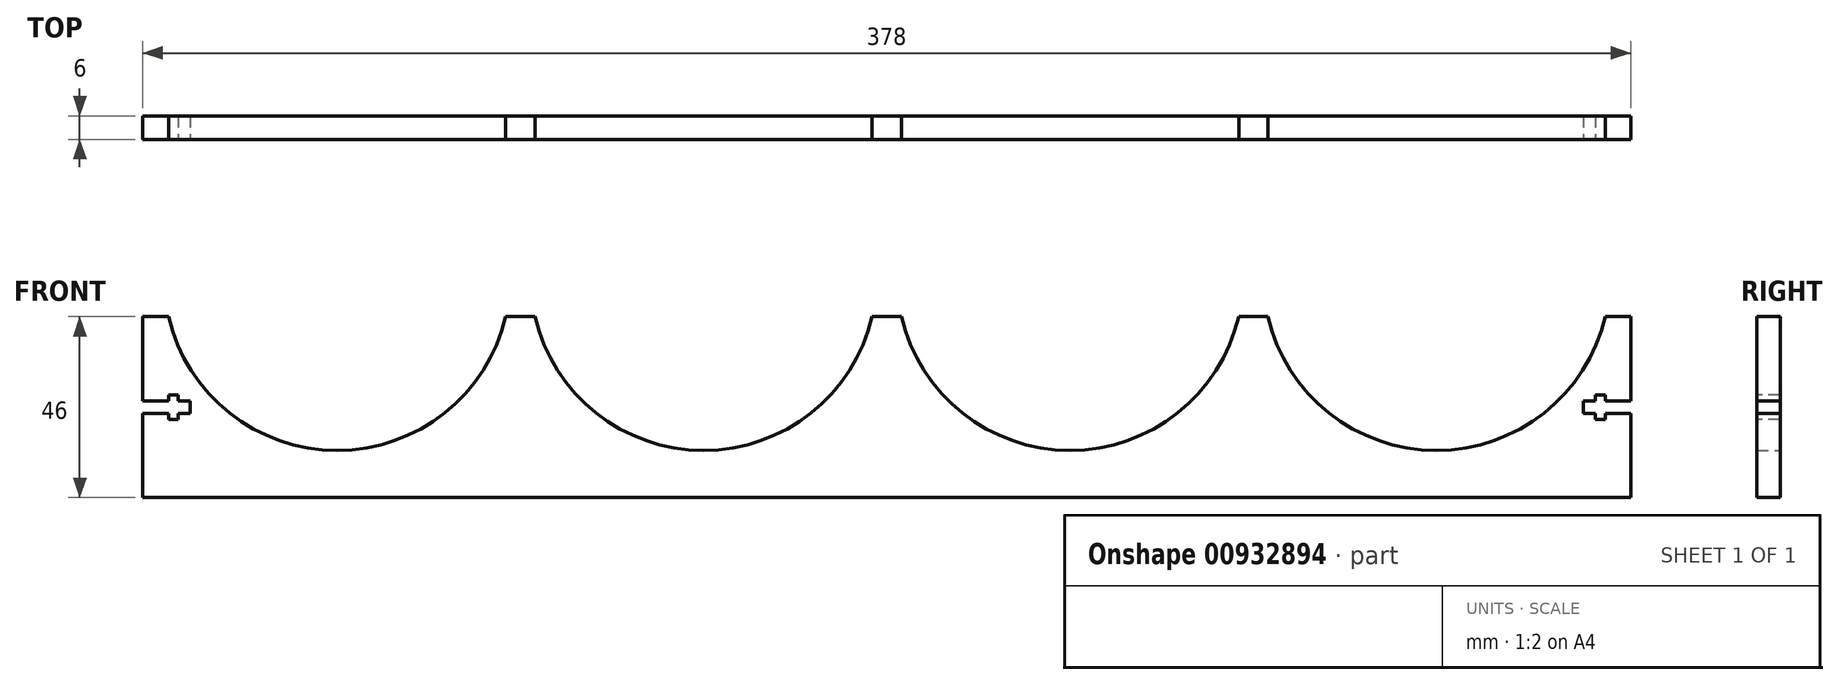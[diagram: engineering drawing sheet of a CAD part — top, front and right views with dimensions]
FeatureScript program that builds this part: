
annotation { "Feature Type Name" : "Feature", "Feature Type Description" : "" }
export const myFeature = defineFeature(function(context is Context, id is Id, definition is map)
    precondition{}
    {
        {
            var Q0;
            Q0=qCreatedBy(makeId("Front.planeOp"),FACE);
            var sketch = newSketch(context, id + "F0", { "sketchPlane" : qUnion([Q0])});
            skLineSegment(sketch, "E0.bottom", {"start": v(-189, 23) * mm, "end": v(-182.5, 23) * mm});
            skLineSegment(sketch, "E0.top", {"start": v(-189, -23) * mm, "end": v(189, -23) * mm});
            skLineSegment(sketch, "E0.left", {"start": v(-189, 23) * mm, "end": v(-189, -23) * mm});
            skLineSegment(sketch, "E0.right", {"start": v(189, 23) * mm, "end": v(189, -23) * mm});
            skLineSegment(sketch, "E1", {"start": v(0, 23) * mm, "end": v(0, 0) * mm, "construction": true});
            skLineSegment(sketch, "E2", {"start": v(0, 0) * mm, "end": v(-189, 0) * mm, "construction": true});
            skArc(sketch, "E3", {"start": v(-182.5, 23) * mm, "mid": v(-139.65, -11) * mm, "end": v(-96.8, 23) * mm});
            skArc(sketch, "E4", {"start": v(-89.4, 23) * mm, "mid": v(-46.55, -11) * mm, "end": v(-3.7, 23) * mm});
            skArc(sketch, "E5.MirrorCS", {"start": v(89.4, 23) * mm, "mid": v(46.55, -11) * mm, "end": v(3.7, 23) * mm});
            skArc(sketch, "E6.MirrorCS", {"start": v(182.5, 23) * mm, "mid": v(139.65, -11) * mm, "end": v(96.8, 23) * mm});
            skLineSegment(sketch, "E7.trimOffspring", {"start": v(-96.8, 23) * mm, "end": v(-89.4, 23) * mm});
            skLineSegment(sketch, "E8.trimOffspring", {"start": v(-3.7, 23) * mm, "end": v(3.7, 23) * mm});
            skLineSegment(sketch, "E9.trimOffspring", {"start": v(89.4, 23) * mm, "end": v(96.8, 23) * mm});
            skLineSegment(sketch, "E10.trimOffspring", {"start": v(182.5, 23) * mm, "end": v(189, 23) * mm});
            skLineSegment(sketch, "E11", {"start": v(-139.65, 33) * mm, "end": v(-46.55, 33) * mm, "construction": true});
            skLineSegment(sketch, "E12", {"start": v(46.55, 33) * mm, "end": v(-46.55, 33) * mm, "construction": true});
            skSolve(sketch);
        }
        {
            var Q0;
            Q0 = qSketchRegion(id + "F0", true);
            extrude(context, id + "F1", {"entities" : qUnion([Q0]), "depth" : 6 * mm, "offsetDistance" : 25 * mm});
        }
        {
            var Q0;
            Q0=makeQuery(id+"F1.opExtrude","CAP_FACE",FACE,{"disambiguationData":[OSD([sQuery(id+"F0.wireOp",EDGE,"E0.bottom"),sQuery(id+"F0.wireOp",EDGE,"E0.top"),sQuery(id+"F0.wireOp",EDGE,"E0.left"),sQuery(id+"F0.wireOp",EDGE,"E0.right"),sQuery(id+"F0.wireOp",EDGE,"E3"),sQuery(id+"F0.wireOp",EDGE,"E4"),sQuery(id+"F0.wireOp",EDGE,"E5.MirrorCS"),sQuery(id+"F0.wireOp",EDGE,"E6.MirrorCS"),sQuery(id+"F0.wireOp",EDGE,"E7.trimOffspring"),sQuery(id+"F0.wireOp",EDGE,"E8.trimOffspring"),sQuery(id+"F0.wireOp",EDGE,"E9.trimOffspring"),sQuery(id+"F0.wireOp",EDGE,"E10.trimOffspring")])],"isStart":false});
            var sketch = newSketch(context, id + "F2", { "sketchPlane" : qUnion([Q0])});
            skLineSegment(sketch, "E13", {"start": v(189, 1.6) * mm, "end": v(182.5, 1.6) * mm});
            skLineSegment(sketch, "E14", {"start": v(182.5, 1.6) * mm, "end": v(182.5, 3.1) * mm});
            skLineSegment(sketch, "E15", {"start": v(182.5, 3.1) * mm, "end": v(180, 3.1) * mm});
            skLineSegment(sketch, "E16", {"start": v(180, 3.1) * mm, "end": v(180, 1.6) * mm});
            skLineSegment(sketch, "E17", {"start": v(180, 1.6) * mm, "end": v(177, 1.6) * mm});
            skLineSegment(sketch, "E18", {"start": v(177, 1.6) * mm, "end": v(177, -1.6) * mm});
            skLineSegment(sketch, "E19", {"start": v(177, 0) * mm, "end": v(189, 0) * mm, "construction": true});
            skLineSegment(sketch, "E20.MirrorCS", {"start": v(189, -1.6) * mm, "end": v(182.5, -1.6) * mm});
            skLineSegment(sketch, "E21.MirrorCS", {"start": v(182.5, -1.6) * mm, "end": v(182.5, -3.1) * mm});
            skLineSegment(sketch, "E22.MirrorCS", {"start": v(182.5, -3.1) * mm, "end": v(180, -3.1) * mm});
            skLineSegment(sketch, "E23.MirrorCS", {"start": v(180, -1.6) * mm, "end": v(177, -1.6) * mm});
            skLineSegment(sketch, "E24.MirrorCS", {"start": v(180, -3.1) * mm, "end": v(180, -1.6) * mm});
            skLineSegment(sketch, "E25", {"start": v(189, 1.6) * mm, "end": v(189, -1.6) * mm});
            skLineSegment(sketch, "E26", {"start": v(0, 0) * mm, "end": v(0, -23) * mm, "construction": true});
            skLineSegment(sketch, "E27.MirrorCS", {"start": v(-177, 1.6) * mm, "end": v(-177, -1.6) * mm});
            skLineSegment(sketch, "E28.MirrorCS", {"start": v(-189, 1.6) * mm, "end": v(-189, -1.6) * mm});
            skLineSegment(sketch, "E29.MirrorCS", {"start": v(-180, -1.6) * mm, "end": v(-177, -1.6) * mm});
            skLineSegment(sketch, "E30.MirrorCS", {"start": v(-182.5, 3.1) * mm, "end": v(-180, 3.1) * mm});
            skLineSegment(sketch, "E31.MirrorCS", {"start": v(-182.5, -1.6) * mm, "end": v(-182.5, -3.1) * mm});
            skLineSegment(sketch, "E32.MirrorCS", {"start": v(-182.5, -3.1) * mm, "end": v(-180, -3.1) * mm});
            skLineSegment(sketch, "E33.MirrorCS", {"start": v(-180, 1.6) * mm, "end": v(-177, 1.6) * mm});
            skLineSegment(sketch, "E34.MirrorCS", {"start": v(-180, -3.1) * mm, "end": v(-180, -1.6) * mm});
            skLineSegment(sketch, "E35.MirrorCS", {"start": v(-182.5, 1.6) * mm, "end": v(-182.5, 3.1) * mm});
            skLineSegment(sketch, "E36.MirrorCS", {"start": v(-180, 3.1) * mm, "end": v(-180, 1.6) * mm});
            skLineSegment(sketch, "E37.MirrorCS", {"start": v(-189, -1.6) * mm, "end": v(-182.5, -1.6) * mm});
            skLineSegment(sketch, "E38.MirrorCS", {"start": v(-189, 1.6) * mm, "end": v(-182.5, 1.6) * mm});
            skSolve(sketch);
        }
        {
            var Q0;
            Q0 = qSketchRegion(id + "F2", true);
            extrude(context, id + "F3", {"entities" : qUnion([Q0]), "operationType" : NewBodyOperationType.REMOVE, "endBound" : BoundingType.THROUGH_ALL, "oppositeDirection" : true, "depth" : 25 * mm, "offsetDistance" : 25 * mm});
        }
    });
